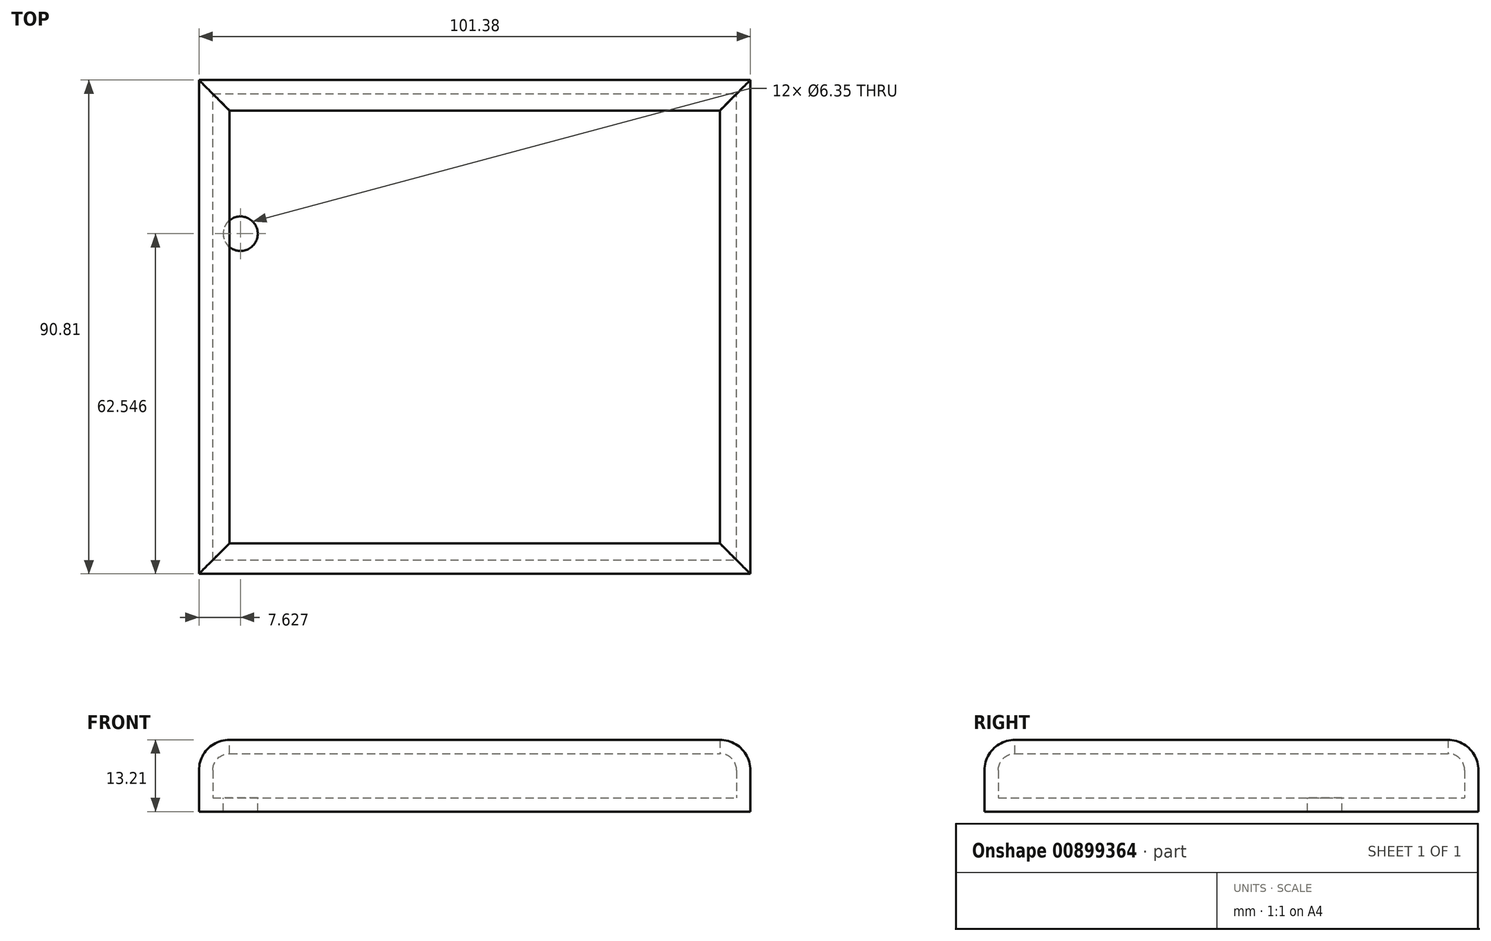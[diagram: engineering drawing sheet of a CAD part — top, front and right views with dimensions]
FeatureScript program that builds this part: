
annotation { "Feature Type Name" : "Feature", "Feature Type Description" : "" }
export const myFeature = defineFeature(function(context is Context, id is Id, definition is map)
    precondition{}
    {
        {
            var Q0;
            Q0=qCreatedBy(makeId("Top.planeOp"),FACE);
            var sketch = newSketch(context, id + "F0", { "sketchPlane" : qUnion([Q0])});
            skLineSegment(sketch, "E0.bottom", {"start": v(-42.05, -36.65) * mm, "end": v(54.25, -36.65) * mm});
            skLineSegment(sketch, "E0.top", {"start": v(-42.05, 49.08) * mm, "end": v(54.25, 49.08) * mm});
            skLineSegment(sketch, "E0.left", {"start": v(-42.05, -36.65) * mm, "end": v(-42.05, 49.08) * mm});
            skLineSegment(sketch, "E0.right", {"start": v(54.25, -36.65) * mm, "end": v(54.25, 49.08) * mm});
            skSolve(sketch);
        }
        {
            var Q0;
            Q0=makeQuery(id+"F0.imprint","IMPRINT",FACE,{"disambiguationData":[TD([[makeQuery(id+"F0.imprint","IMPRINT",EDGE,{"derivedFrom":sQuery(id+"F0.wireOp",EDGE,"E0.bottom")}),1.0]])]});
            extrude(context, id + "F1", {"entities" : qUnion([Q0]), "depth" : 8.13 * mm, "offsetDistance" : 25.4 * mm});
        }
        {
            var Q0;
            Q0=makeQuery(id+"F1.opExtrude","CAP_EDGE",EDGE,{"disambiguationData":[OSD([sQuery(id+"F0.wireOp",EDGE,"E0.bottom")])],"isStart":false});
            var Q1;
            Q1=makeQuery(id+"F1.opExtrude","CAP_EDGE",EDGE,{"disambiguationData":[OSD([sQuery(id+"F0.wireOp",EDGE,"E0.top")])],"isStart":false});
            var Q2;
            Q2=makeQuery(id+"F1.opExtrude","CAP_EDGE",EDGE,{"disambiguationData":[OSD([sQuery(id+"F0.wireOp",EDGE,"E0.left")])],"isStart":false});
            var Q3;
            Q3=makeQuery(id+"F1.opExtrude","CAP_EDGE",EDGE,{"disambiguationData":[OSD([sQuery(id+"F0.wireOp",EDGE,"E0.right")])],"isStart":false});
            fillet(context, id + "F2", {"entities" : qUnion([Q0, Q1, Q2, Q3]), "radius" : 3.07 * mm, "tangentPropagation" : true, "allowEdgeOverflow" : false});
        }
        {
            var Q0;
            Q0=makeQuery(id+"F1.opExtrude","CAP_FACE",FACE,{"disambiguationData":[OSD([sQuery(id+"F0.wireOp",EDGE,"E0.bottom"),sQuery(id+"F0.wireOp",EDGE,"E0.top"),sQuery(id+"F0.wireOp",EDGE,"E0.left"),sQuery(id+"F0.wireOp",EDGE,"E0.right")])],"isStart":false});
            shell(context, id + "F3", {"entities" : qUnion([Q0]), "thickness" : 2.54 * mm, "oppositeDirection" : true});
        }
        {
            var Q0;
            Q0=makeQuery(id+"F3.opShell","OFFSET_FACE",FACE,{"disambiguationData":[OSD([sQuery(id+"F0.wireOp",EDGE,"E0.bottom"),sQuery(id+"F0.wireOp",EDGE,"E0.top"),sQuery(id+"F0.wireOp",EDGE,"E0.left"),sQuery(id+"F0.wireOp",EDGE,"E0.right")])]});
            var sketch = newSketch(context, id + "F4", { "sketchPlane" : qUnion([Q0])});
            skCircle(sketch, "E1", {"center": v(-36.96, 23.36) * mm, "radius": 4.22 * mm});
            skCircle(sketch, "E2", {"center": v(-36.96, 23.36) * mm, "radius": 5.48 * mm});
            skSolve(sketch);
        }
        {
            var Q0;
            Q0=sQuery(id+"F4.wireOp",VERTEX,"E1.center");
            var Q1;
            Q1=makeQuery(id+"F1.opExtrude","SWEPT_BODY",BODY,{"disambiguationData":[OSD([sQuery(id+"F0.wireOp",EDGE,"E0.bottom"),sQuery(id+"F0.wireOp",EDGE,"E0.top"),sQuery(id+"F0.wireOp",EDGE,"E0.left"),sQuery(id+"F0.wireOp",EDGE,"E0.right")])]});
            hole(context, id + "F5", {"style" : HoleStyle.SIMPLE, "endStyle" : HoleEndStyle.THROUGH, "holeDiameter" : 6.35 * mm, "majorDiameter" : 6.35 * mm, "isTappedThrough" : true, "tappedDepth" : 12.7 * mm, "tapClearance" : 3, "locations" : qUnion([Q0]), "scope" : qUnion([Q1])});
        }
    });
